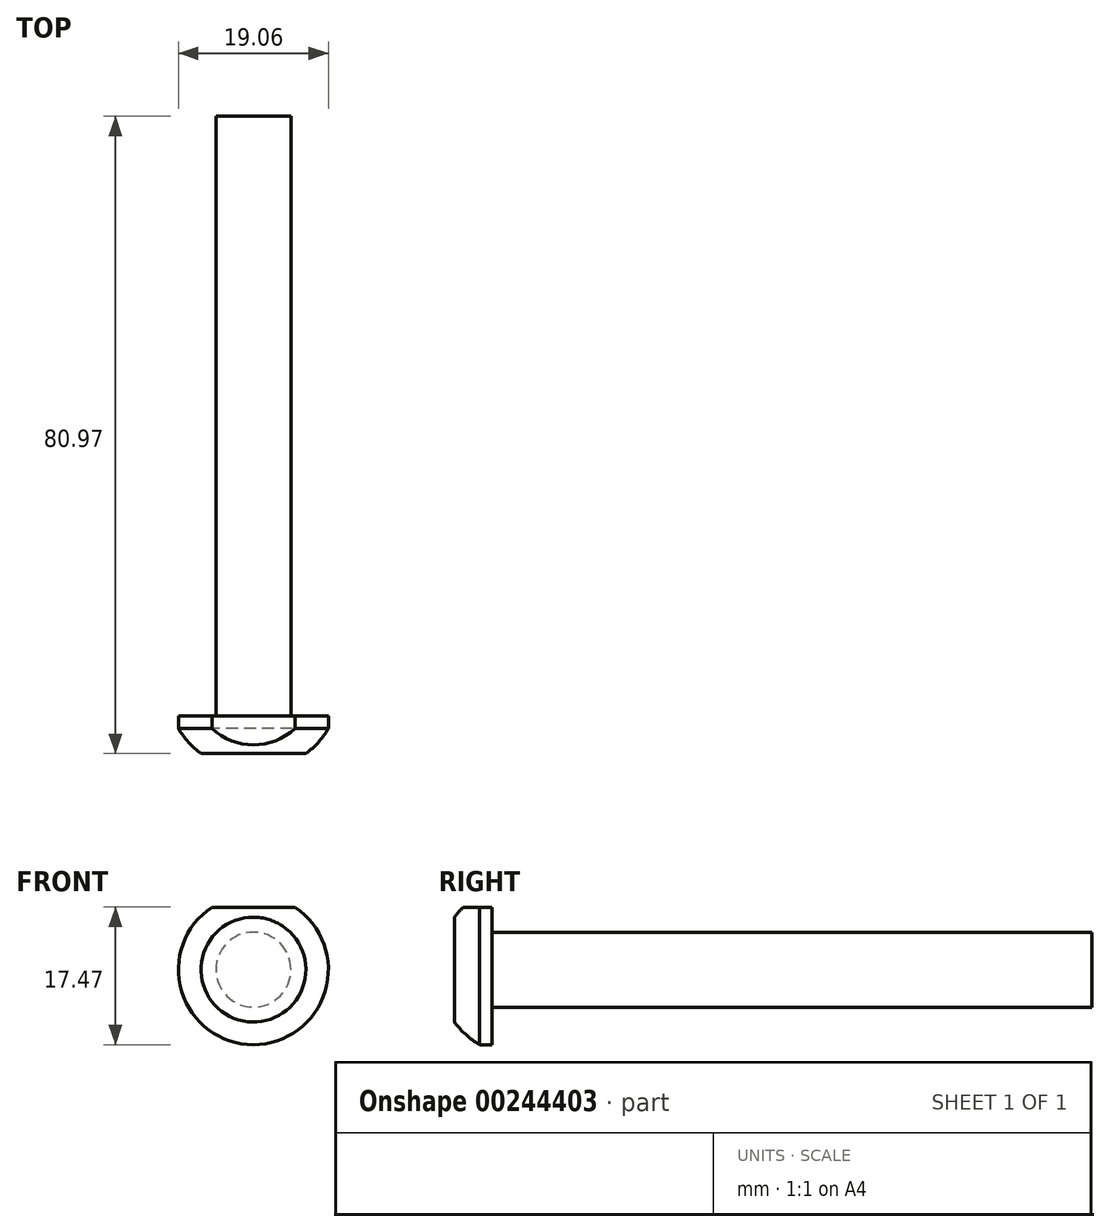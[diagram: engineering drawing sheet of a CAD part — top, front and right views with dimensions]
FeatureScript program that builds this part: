
annotation { "Feature Type Name" : "Feature", "Feature Type Description" : "" }
export const myFeature = defineFeature(function(context is Context, id is Id, definition is map)
    precondition{}
    {
        {
            var Q0;
            Q0=qCreatedBy(makeId("Right.planeOp"),FACE);
            var sketch = newSketch(context, id + "F0", { "sketchPlane" : qUnion([Q0])});
            skLineSegment(sketch, "E0", {"start": v(0, 0) * mm, "end": v(-44.84, 0) * mm});
            skLineSegment(sketch, "E1", {"start": v(-50.56, -9.53) * mm, "end": v(-48.97, -9.53) * mm});
            skLineSegment(sketch, "E2", {"start": v(-48.97, -9.52) * mm, "end": v(-48.97, 0) * mm});
            skLineSegment(sketch, "E3", {"start": v(-48.97, 0) * mm, "end": v(-48.97, -4.76) * mm});
            skLineSegment(sketch, "E4", {"start": v(-48.97, -4.76) * mm, "end": v(27.23, -4.76) * mm});
            skLineSegment(sketch, "E5", {"start": v(27.23, -4.76) * mm, "end": v(27.23, 0) * mm});
            skLineSegment(sketch, "E6", {"start": v(27.23, 0) * mm, "end": v(-48.97, 0) * mm});
            skLineSegment(sketch, "E7", {"start": v(-48.97, 0) * mm, "end": v(-53.74, 0) * mm});
            skLineSegment(sketch, "E8", {"start": v(-53.74, 0) * mm, "end": v(-53.74, -6.66) * mm});
            skArc(sketch, "E9.trimOffspring", {"start": v(-53.74, -6.66) * mm, "mid": v(-52.29, -8.24) * mm, "end": v(-50.56, -9.52) * mm});
            skSolve(sketch);
        }
        {
            var Q0;
            Q0 = qSketchRegion(id + "F0", true);
            var Q1;
            Q1=sQuery(id+"F0.wireOp",EDGE,"E6");
            revolve(context, id + "F1", {"entities" : qUnion([Q0]), "axis" : qUnion([Q1]), "revolveType" : RevolveType.FULL});
        }
        {
            var Q0;
            Q0=makeQuery(id+"F1.opRevolve","SWEPT_FACE",FACE,{"disambiguationData":[OSD([sQuery(id+"F0.wireOp",EDGE,"E2")])]});
            var sketch = newSketch(context, id + "F2", { "sketchPlane" : qUnion([Q0])});
            skLineSegment(sketch, "E10", {"start": v(0, 0) * mm, "end": v(0, 7.94) * mm});
            skLineSegment(sketch, "E11", {"start": v(0, 7.94) * mm, "end": v(5.27, 7.94) * mm});
            skLineSegment(sketch, "E12", {"start": v(5.27, 7.94) * mm, "end": v(-5.27, 7.94) * mm});
            skSolve(sketch);
        }
        {
            var Q0;
            {var subQ0=sQuery(id+"F2.wireOp",EDGE,"E12");var subQ1=makeQuery(id+"F2.imprint","IMPRINT",VERTEX,{"derivedFrom":subQ0});Q0=makeQuery(id+"F2.imprint","IMPRINT",FACE,{"disambiguationData":[TD([[makeQuery(id+"F2.imprint","IMPRINT",EDGE,{"disambiguationData":[TD([[subQ1,1.0]])],"derivedFrom":subQ0}),-1.0]])]});}
            extrude(context, id + "F3", {"entities" : qUnion([Q0]), "operationType" : NewBodyOperationType.REMOVE, "endBound" : BoundingType.THROUGH_ALL, "oppositeDirection" : true, "depth" : 25.4 * mm});
        }
    });
